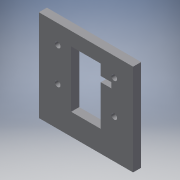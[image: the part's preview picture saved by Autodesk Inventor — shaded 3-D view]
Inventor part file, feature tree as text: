
AUTODESK INVENTOR PART (.ipt)
format: ipt  version: 2018 (Build 220112000, 112)  size: 189,440 bytes
history: native  units: in
note: dims shown in document units (in); Inventor stores cm internally (conversion verified against a paired STEP export)
features: reference x21, other x8, extrude x4, sketch x4, plane x1, mirror x1
ambient origin geometry x8: Origin, YZ Plane, XZ Plane, XY Plane, X Axis, Y Axis, Z Axis, Center Point
bodies: Solid1 (feature_tree)
feature tree (39):
  extrude  "Extrusion1"  Depth=0.1969in
  extrude  "Extrusion2"  Depth=0.1969in
  extrude  "Extrusion3"  Depth=0.1969in
  plane  "Work Plane1"
  mirror  "Mirror1"
  extrude  "Extrusion4"  Depth=0.1181in
  sketch  "Sketch1"  dims[d0=0.1969in d1=0.1969in]
  reference  "Reference1"
  reference  "Reference2"
  reference  "Reference3"
  reference  "Reference4"
  reference  "Reference5"
  reference  "Reference6"
  reference  "Reference7"
  reference  "Reference8"
  reference  "Reference9"
  sketch  "Sketch2"  dims[d2=1.378in d3=0.1969in]
  reference  "Reference10"
  reference  "Reference11"
  reference  "Reference12"
  reference  "Reference13"
  reference  "Reference14"
  reference  "Reference15"
  reference  "Reference16"
  reference  "Reference17"
  sketch  "Sketch3"  dims[d4=0.1969in d5=0.2756in]
  sketch  "Sketch4"  dims[d6=0.2756in d7=0.1181in d8=0.7087in d9=0.1201in d10=0.1575in d11=0.1181in d12=0.0in d13=0.1969in d14=0.0394in d15=0.2047in d16=0.2047in d17=0.1181in d18=0.1181in d19=0.0in d20=0.5906in d21=0.5512in d22=0.5512in d23=0.1181in d24=0.1969in d25=0.1969in d26=0.1181in d27=0.0in d28=0.5556in d29=0.0in]
  reference  "Reference18"
  reference  "Reference19"
  reference  "Reference20"
  reference  "Reference21"
  other  "Assembly2"
  other  "Raspberry Pi Camera v1.3:1"
  other  "Lepton 3 thermal camera:1"
  other  "Breakout Board:1"
  other  "Angle bracket short:1"
  other  "Angle bracket short:2"
  other  "Angle bracket short:4"
  other  "Angle bracket short:3"
